# Revit family: UR-Ouro Arm Mount
name_source: partatom
category: Lighting Fixtures
units: mm (PartAtom-declared; Revit-internal decimal feet)

## family parameters
Cut with Voids When Loaded = No
Host = Face
Light Source = Yes
OmniClass Number = 23.80.70.14.21
OmniClass Title = Street and Roadway Lighting
Part Type = Normal
Room Calculation Point = No
Round Connector Dimension = Use Diameter
Shared = No

## types (6) — shared parameters
Color Filter = 16777215
Default Elevation = 48 "
Description = Ouro is a seamless blend of elegant form, performance, visual comfort, controls, scalability and mounting options to enhance the environment in which they occupy
Dimming Lamp Color Temperature Shift = <None>
Emit Shape Visible in Rendering = No
Glass = White Glass
Lamp = Ouro ™ LED
Load Classification = Lighting
Manufacturer = KIM Lighting
Photometric Note = Photometric Web Files dowload in the Web link
Power Factor = 1
Product Material = Black
Tilt Angle = 90.00°
URL = https://www.currentlighting.com
Voltage = 120 V

## per-type parameters (varying)
| type | Apparent Load | CCT | Distribution | Emit from Circle Diameter | LED Engine | Lens | Model | Photometric Web File | UR20 | UR28 | Wattage Comments | Watts | zz Height 1 | zz Height 2 | zz Length 1 | zz Length 2 | zz Radius 1 |
| UR28-96L-315-4K7-5R | 315 VA | 4K7-4000K, 70 CRI | 5R - Type V Rectangular | 25.5 " | 96L-315 | Clear Lens | KIM UR28 | UR28-96L-315-4K7-5R.IES | No | Yes | Ouro 28 delivers up to 35,000 lumens | 315 W | 5.9 " | 4.4 " | 28 " | 4.9 " | 12.75 " |
| UR28-96L-170-3K7-4 | 170 VA | 3K7 3000K, 70 CRI | 4 - Type IV | 25.5 " | 96L-170 | No Lens | KIM UR28 | UR28-96L-170-3K7-4.IES | No | Yes | Ouro 28 delivers up to 35,000 lumens | 170 W | 5.9 " | 4.4 " | 28 " | 4.9 " | 12.75 " |
| UR28-96L-185-5K7-FR | 185 VA | 5K7-5000K, 70 CRI | FR-Type 1/Front Row | 25.5 " | 96L-185 | Clear Lens | KIM UR28 | UR28-96L-185-5K7-FR.IES | No | Yes | Ouro 28 delivers up to 35,000 lumens | 185 W | 5.9 " | 4.4 " | 28 " | 4.9 " | 12.75 " |
| UR20-24L-65-4K7-5QM | 65 VA | 4K7-4000K, 70 CRI | 5QM-Type V Square Medium | 17.5 " | 24L-65 | Clear Lens | KIM UR20 | UR20-24L-65-4K7-5QM.IES | Yes | No | Ouro 20 delivers up to 17,000 lumens | 65 W | 5.7 " | 3.5 " | 20 " | 4.8 " | 8.75 " |
| UR20-24L-25-4K7-5R-CLR | 25 VA | 4K7-4000K, 70 CRI | 5R-Type V Rectangular | 17.5 " | 24L-25 | Clear Lens | KIM UR20 | UR20-24L-25-4K7-5R-CLR.IES | Yes | No | Ouro 20 delivers up to 17,000 lumens | 25 W | 5.7 " | 3.5 " | 20 " | 4.8 " | 8.75 " |
| UR20-68L-150-5K7-3 | 150 VA | 5K7-5000K, 70 CRI | 3-Type III | 17.5 " | 68L-150 | High Diffusion Lens | KIM UR20 | UR20-68L-150-5K7-3.IES | Yes | No | Ouro 20 delivers up to 17,000 lumens | 150 W | 5.7 " | 3.5 " | 20 " | 4.8 " | 8.75 " |

## geometry (parser evidence)
native form markers: Sweep x1
no freeform markers — native parametric forms only
